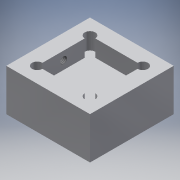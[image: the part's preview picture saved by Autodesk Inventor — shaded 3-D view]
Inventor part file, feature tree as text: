
AUTODESK INVENTOR PART (.ipt)
format: ipt  version: 2017 (Build 210142000, 142)  size: 163,840 bytes
history: native  units: mm
features: sketch x7, hole x4, extrude x3, projected_geometry x3
ambient origin geometry x8: Origin, YZ Plane, XZ Plane, XY Plane, X Axis, Y Axis, Z Axis, Center Point
bodies: Solid1 (feature_tree)
feature tree (17):
  extrude  "Extrusion1"  Depth=40.0mm
  hole  "Hole2"  [1 undecoded]
  extrude  "Extrusion3"  Depth=8.0mm TaperAngle=0.0deg
  hole  "Hole3"  [1 undecoded]
  extrude  "Extrusion4"  Depth=6.0mm TaperAngle=0.0deg
  hole  "Hole5"  [1 undecoded]
  hole  "Hole6"  [1 undecoded]
  sketch  "Sketch1"  dims[d0=40.0mm d1=40.0mm]
  sketch  "Sketch4"  dims[d2=20.0mm d3=0.0mm d15=25.2mm]
  sketch  "Sketch5"  dims[d16=25.2mm]
  sketch  "Sketch6"  dims[d17=5.0mm d18=6.0mm d19=4.0mm d20=2.0mm d21=90.0deg d22=8.0mm d23=0.0mm d24=8.0mm d25=0.0mm]
  projected_geometry  "Projected Loop1"
  sketch  "Sketch8"  dims[d27=20.0mm]
  projected_geometry  "Projected Loop2"
  sketch  "Sketch9"  dims[d28=3.242mm d29=8.0mm d30=4.0mm d31=2.0mm d32=90.0deg d33=11.8mm d34=20.594885mm d44=25.0mm]
  projected_geometry  "Projected Loop3"
  sketch  "Sketch10"  dims[d45=25.0mm d46=6.0mm d47=0.0mm d48=3.0mm d49=6.0mm d50=4.0mm d51=2.0mm d52=90.0deg d53=6.0mm d54=0.0mm d55=3.242mm d56=8.0mm d57=4.0mm d58=2.0mm d59=90.0deg d60=4.0mm d61=20.594885mm]
note: 4 required parameter values undecoded (feature->parameter linkage not recoverable at this tier; creation-order binding heuristic only, values carry confidence <= 0.55)
